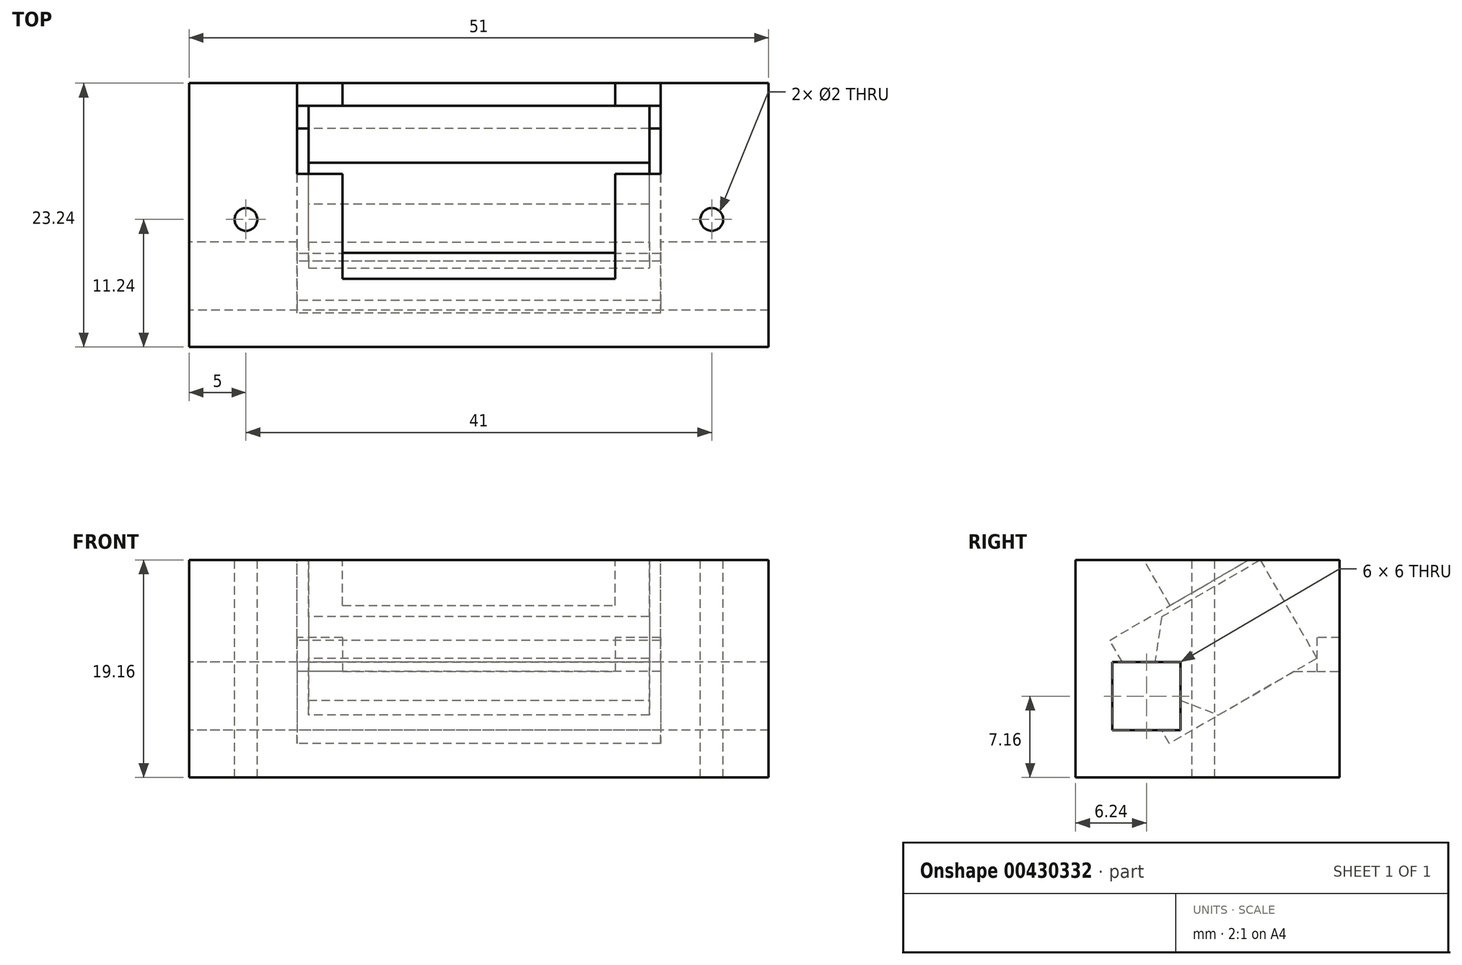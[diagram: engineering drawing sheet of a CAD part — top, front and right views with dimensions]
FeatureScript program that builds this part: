
annotation { "Feature Type Name" : "Feature", "Feature Type Description" : "" }
export const myFeature = defineFeature(function(context is Context, id is Id, definition is map)
    precondition{}
    {
        {
            assignVariable(context, id + "F0", {"name" : "Breite", "anyValue" : 30});
        }
        {
            var Q0;
            Q0=qCreatedBy(makeId("Right.planeOp"),FACE);
            var sketch = newSketch(context, id + "F1", { "sketchPlane" : qUnion([Q0])});
            skLineSegment(sketch, "E0.bottom", {"start": v(-8.66, -5) * mm, "end": v(0, 0) * mm});
            skLineSegment(sketch, "E0.top", {"start": v(-3.66, -13.66) * mm, "end": v(5, -8.66) * mm});
            skLineSegment(sketch, "E0.left", {"start": v(-8.66, -5) * mm, "end": v(-3.66, -13.66) * mm});
            skLineSegment(sketch, "E0.right", {"start": v(0, 0) * mm, "end": v(5, -8.66) * mm});
            skLineSegment(sketch, "E1", {"start": v(-8.66, -5) * mm, "end": v(-9.62, -11.33) * mm});
            skLineSegment(sketch, "E2", {"start": v(-9.62, -11.33) * mm, "end": v(-3.66, -13.66) * mm});
            skSolve(sketch);
        }
        {
            var Q0;
            Q0=qSketchRegion(id+"F1",true);
            extrude(context, id + "F2", {"entities" : qUnion([Q0]), "depth" : (getVariable(context, 'Breite')) * mm, "offsetDistance" : 25 * mm, "symmetric" : true});
        }
        {
            var Q0;
            Q0=qCreatedBy(makeId("Right.planeOp"),FACE);
            var sketch = newSketch(context, id + "F3", { "sketchPlane" : qUnion([Q0])});
            skLineSegment(sketch, "E3.bottom", {"start": v(-16.24, 0) * mm, "end": v(-1, 0) * mm});
            skLineSegment(sketch, "E3.top", {"start": v(-16.24, -19.16) * mm, "end": v(7, -19.16) * mm});
            skLineSegment(sketch, "E3.left", {"start": v(-16.24, 0) * mm, "end": v(-16.24, -19.16) * mm});
            skLineSegment(sketch, "E3.right", {"start": v(7, -9.81) * mm, "end": v(7, -19.16) * mm});
            skLineSegment(sketch, "E4", {"start": v(3, -9.81) * mm, "end": v(-8, -16.16) * mm});
            skLineSegment(sketch, "E5", {"start": v(-8, -16.16) * mm, "end": v(-13.24, -7.07) * mm});
            skLineSegment(sketch, "E6", {"start": v(-13.24, -7.07) * mm, "end": v(-1, 0) * mm});
            skLineSegment(sketch, "E7", {"start": v(3, -9.81) * mm, "end": v(7, -9.81) * mm});
            skLineSegment(sketch, "E8", {"start": v(-7.93, -4) * mm, "end": v(-10.24, 0) * mm});
            skLineSegment(sketch, "E9.bottom", {"start": v(7, -6.81) * mm, "end": v(5, -6.81) * mm});
            skLineSegment(sketch, "E9.left", {"start": v(7, -6.81) * mm, "end": v(7, -9.81) * mm});
            skLineSegment(sketch, "E9.right", {"start": v(5, -6.81) * mm, "end": v(5, -9.81) * mm});
            skSolve(sketch);
        }
        {
            var Q0;
            Q0=qSketchRegion(id+"F3",true);
            extrude(context, id + "F4", {"entities" : qUnion([Q0]), "depth" : (getVariable(context, 'Breite') + 2) * mm, "offsetDistance" : 25 * mm, "symmetric" : true});
        }
        {
            var Q0;
            {var subQ3=sQuery(id+"F3.wireOp",EDGE,"E8");Q0=makeQuery(id+"F3.imprint","IMPRINT",FACE,{"disambiguationData":[TD([[makeQuery(id+"F3.imprint","IMPRINT",EDGE,{"derivedFrom":subQ3}),-1.0]])]});}
            var Q1;
            Q1=makeQuery(id+"F3.imprint","IMPRINT",FACE,{"disambiguationData":[TD([[makeQuery(id+"F3.imprint","IMPRINT",EDGE,{"derivedFrom":sQuery(id+"F3.wireOp",EDGE,"E9.bottom")}),1.0]])]});
            extrude(context, id + "F5", {"entities" : qUnion([Q0, Q1]), "operationType" : NewBodyOperationType.REMOVE, "oppositeDirection" : true, "depth" : (getVariable(context, 'Breite') - 6) * mm, "offsetDistance" : 25 * mm, "symmetric" : true});
        }
        {
            var Q0;
            Q0=makeQuery(id+"F4.opExtrude","SWEPT_FACE",FACE,{"disambiguationData":[OSD([sQuery(id+"F3.wireOp",EDGE,"E3.bottom")])]});
            var sketch = newSketch(context, id + "F6", { "sketchPlane" : qUnion([Q0])});
            skCircle(sketch, "E10", {"center": v(20.5, -5) * mm, "radius": 1 * mm});
            skLineSegment(sketch, "E11.bottom", {"start": v(16, -16.24) * mm, "end": v(25.5, -16.24) * mm});
            skLineSegment(sketch, "E11.top", {"start": v(16, 7) * mm, "end": v(25.5, 7) * mm});
            skLineSegment(sketch, "E11.left", {"start": v(16, -16.24) * mm, "end": v(16, 7) * mm});
            skLineSegment(sketch, "E11.right", {"start": v(25.5, -16.24) * mm, "end": v(25.5, 7) * mm});
            skLineSegment(sketch, "E12.MirrorCS", {"start": v(-16, -16.24) * mm, "end": v(-25.5, -16.24) * mm});
            skLineSegment(sketch, "E13.MirrorCS", {"start": v(-25.5, -16.24) * mm, "end": v(-25.5, 7) * mm});
            skLineSegment(sketch, "E14.MirrorCS", {"start": v(-16, -16.24) * mm, "end": v(-16, 7) * mm});
            skLineSegment(sketch, "E15.MirrorCS", {"start": v(-16, 7) * mm, "end": v(-25.5, 7) * mm});
            skCircle(sketch, "E16.MirrorC", {"center": v(-20.5, -5) * mm, "radius": 1 * mm});
            skSolve(sketch);
        }
        {
            var Q0;
            Q0=qSketchRegion(id+"F6",true);
            var Q1;
            Q1=makeQuery(id+"F4.opExtrude","SWEPT_FACE",FACE,{"disambiguationData":[OSD([sQuery(id+"F3.wireOp",EDGE,"E3.top")])]});
            extrude(context, id + "F7", {"entities" : qUnion([Q0]), "operationType" : NewBodyOperationType.ADD, "endBound" : BoundingType.UP_TO_SURFACE, "oppositeDirection" : true, "depth" : 25 * mm, "endBoundEntityFace" : qUnion([Q1]), "offsetDistance" : 25 * mm});
        }
        {
            var Q0;
            Q0=makeQuery(id+"F7.opExtrude","SWEPT_FACE",FACE,{"disambiguationData":[OSD([sQuery(id+"F6.wireOp",EDGE,"E13.MirrorCS")])]});
            var sketch = newSketch(context, id + "F8", { "sketchPlane" : qUnion([Q0])});
            skLineSegment(sketch, "E17.bottom", {"start": v(13, -15) * mm, "end": v(7, -15) * mm});
            skLineSegment(sketch, "E17.top", {"start": v(13, -9) * mm, "end": v(7, -9) * mm});
            skLineSegment(sketch, "E17.left", {"start": v(13, -15) * mm, "end": v(13, -9) * mm});
            skLineSegment(sketch, "E17.right", {"start": v(7, -15) * mm, "end": v(7, -9) * mm});
            skPoint(sketch, "E17.middle", {"position": v(10, -12) * mm});
            skSolve(sketch);
        }
        {
            var Q0;
            Q0=qSketchRegion(id+"F8",true);
            extrude(context, id + "F9", {"entities" : qUnion([Q0]), "operationType" : NewBodyOperationType.REMOVE, "endBound" : BoundingType.THROUGH_ALL, "oppositeDirection" : true, "depth" : 25 * mm, "offsetDistance" : 25 * mm});
        }
    });
